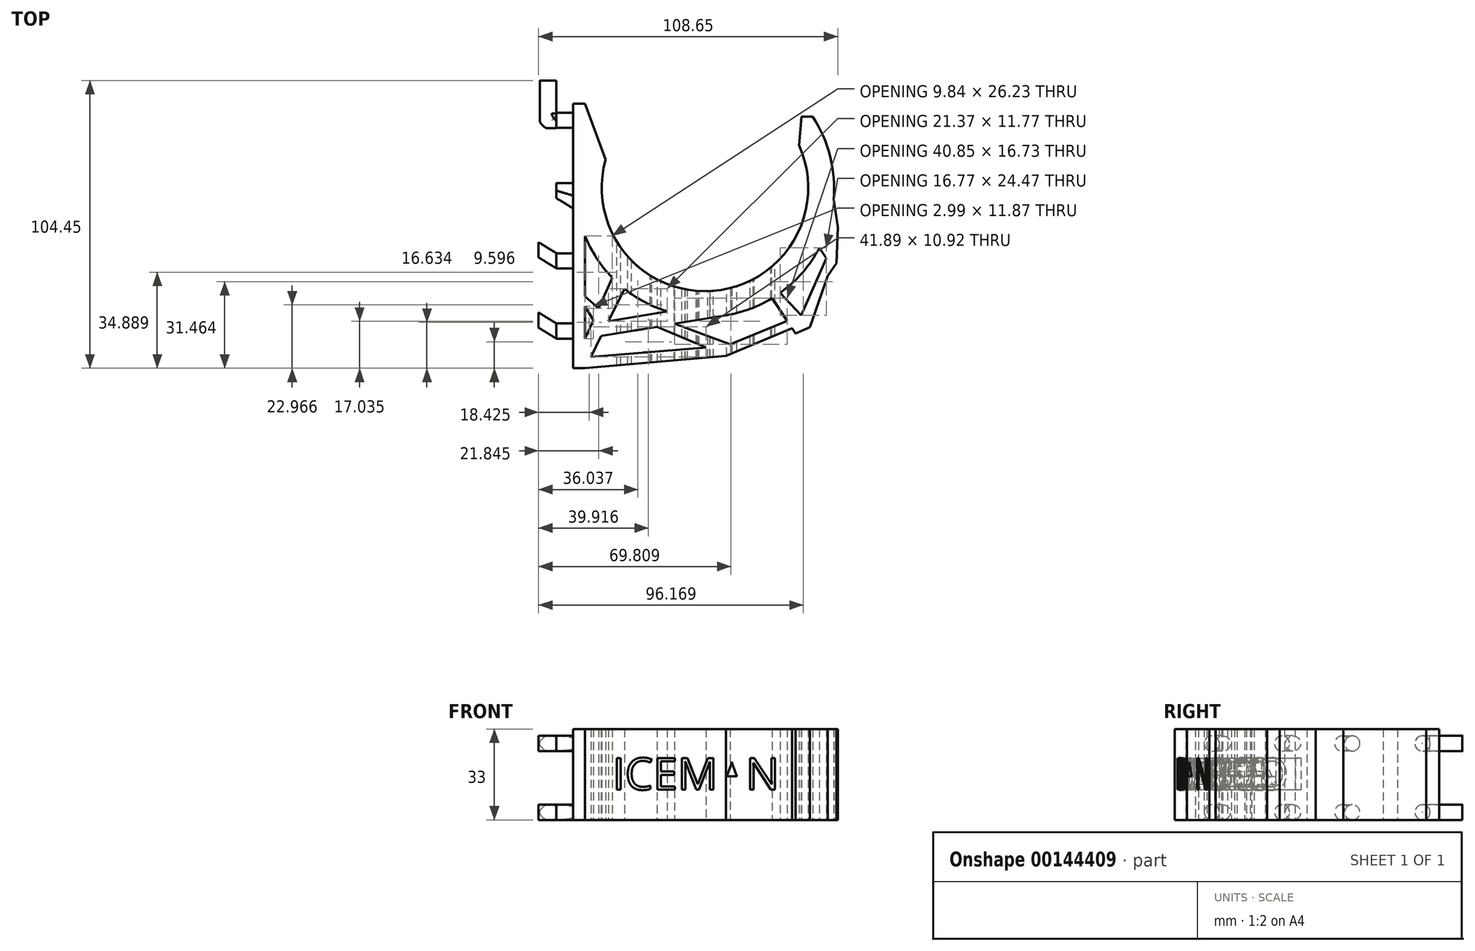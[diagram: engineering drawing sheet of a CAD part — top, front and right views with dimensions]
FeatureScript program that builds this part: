
annotation { "Feature Type Name" : "Feature", "Feature Type Description" : "" }
export const myFeature = defineFeature(function(context is Context, id is Id, definition is map)
    precondition{}
    {
        {
            var Q0;
            Q0=qCreatedBy(makeId("Top.planeOp"),FACE);
            var sketch = newSketch(context, id + "F0", { "sketchPlane" : qUnion([Q0])});
            skLineSegment(sketch, "E0.top", {"start": v(0, 33.67) * mm, "end": v(4.44, 33.67) * mm});
            skLineSegment(sketch, "E0.left", {"start": v(0, 0) * mm, "end": v(0, 33.67) * mm});
            skLineSegment(sketch, "E0.right", {"start": v(4.44, -16.05) * mm, "end": v(4.44, -14.33) * mm});
            skArc(sketch, "E1", {"start": v(11.88, 13.42) * mm, "mid": v(50.67, -34.27) * mm, "end": v(82.12, 18.55) * mm});
            skArc(sketch, "E2", {"start": v(4.44, -14.33) * mm, "mid": v(16.23, -31.39) * mm, "end": v(34.23, -41.69) * mm});
            skLineSegment(sketch, "E3", {"start": v(4.44, 33.67) * mm, "end": v(11.88, 13.42) * mm});
            skLineSegment(sketch, "E4", {"start": v(83.02, 29.02) * mm, "end": v(87.01, 29.02) * mm});
            skLineSegment(sketch, "E5.top", {"start": v(0, -62.33) * mm, "end": v(4.44, -62.33) * mm});
            skLineSegment(sketch, "E5.left", {"start": v(0, 33.67) * mm, "end": v(0, -62.33) * mm});
            skLineSegment(sketch, "E5.right", {"start": v(4.44, -14.33) * mm, "end": v(4.44, -36.24) * mm});
            skLineSegment(sketch, "E6", {"start": v(14.27, -29.48) * mm, "end": v(9.36, -40.56) * mm});
            skLineSegment(sketch, "E7", {"start": v(10.19, -50.67) * mm, "end": v(30.6, -47.27) * mm});
            skLineSegment(sketch, "E8", {"start": v(55.64, -43.1) * mm, "end": v(76.36, -43.1) * mm});
            skLineSegment(sketch, "E9", {"start": v(83.02, 29.02) * mm, "end": v(82.12, 18.55) * mm});
            skLineSegment(sketch, "E10", {"start": v(18.67, -33.48) * mm, "end": v(12.86, -45.25) * mm});
            skLineSegment(sketch, "E11", {"start": v(12.86, -45.25) * mm, "end": v(34.23, -41.69) * mm});
            skLineSegment(sketch, "E12", {"start": v(36.9, -46.22) * mm, "end": v(57.12, -53.66) * mm});
            skLineSegment(sketch, "E13", {"start": v(48.37, -54.8) * mm, "end": v(30.6, -47.27) * mm});
            skLineSegment(sketch, "E14", {"start": v(30.6, -47.27) * mm, "end": v(48.37, -54.8) * mm});
            skLineSegment(sketch, "E15", {"start": v(57.12, -53.66) * mm, "end": v(77.74, -45.18) * mm});
            skLineSegment(sketch, "E16.trimOffspring", {"start": v(36.9, -46.22) * mm, "end": v(55.64, -43.1) * mm});
            skArc(sketch, "E17.trimOffspring", {"start": v(55.64, -43.1) * mm, "mid": v(64.25, -40.8) * mm, "end": v(72.27, -36.93) * mm});
            skLineSegment(sketch, "E18", {"start": v(82.8, -43.1) * mm, "end": v(75.3, -34.93) * mm});
            skLineSegment(sketch, "E19", {"start": v(72.27, -36.93) * mm, "end": v(77.74, -45.18) * mm});
            skLineSegment(sketch, "E20", {"start": v(86.04, -47.4) * mm, "end": v(92.47, -28.8) * mm});
            skLineSegment(sketch, "E21", {"start": v(97.82, -6.72) * mm, "end": v(94.7, 0) * mm});
            skLineSegment(sketch, "E22", {"start": v(89.45, -18.63) * mm, "end": v(92.06, -22.39) * mm});
            skLineSegment(sketch, "E23.trimOffspring", {"start": v(79.52, -47.86) * mm, "end": v(80.77, -49.75) * mm});
            skLineSegment(sketch, "E24", {"start": v(97.82, -6.72) * mm, "end": v(93.84, -6.35) * mm});
            skLineSegment(sketch, "E25", {"start": v(7.43, -44.89) * mm, "end": v(4.44, -39.76) * mm});
            skLineSegment(sketch, "E26", {"start": v(4.44, -36.24) * mm, "end": v(9.36, -40.56) * mm});
            skLineSegment(sketch, "E27", {"start": v(94.62, -1.13) * mm, "end": v(96.16, -11.08) * mm});
            skLineSegment(sketch, "E28", {"start": v(95.7, -24.2) * mm, "end": v(94.3, -26.43) * mm});
            skLineSegment(sketch, "E29", {"start": v(96.16, -11.08) * mm, "end": v(95.7, -24.2) * mm});
            skPoint(sketch, "E30.orphan", {"position": v(97.7, -21.03) * mm});
            skArc(sketch, "E31.trimOffspring", {"start": v(94.62, -1.13) * mm, "mid": v(93.39, 14.6) * mm, "end": v(87.01, 29.02) * mm});
            skArc(sketch, "E32.trimOffspring", {"start": v(94.7, 0) * mm, "mid": v(1.5, 9.46) * mm, "end": v(93.84, -6.35) * mm});
            skLineSegment(sketch, "E33", {"start": v(82.8, -43.1) * mm, "end": v(92.06, -22.39) * mm});
            skLineSegment(sketch, "E34", {"start": v(92.47, -28.8) * mm, "end": v(95.7, -24.2) * mm});
            skLineSegment(sketch, "E35.trimOffspring", {"start": v(79.52, -47.86) * mm, "end": v(55.58, -57.85) * mm});
            skLineSegment(sketch, "E36", {"start": v(80.77, -49.75) * mm, "end": v(86.04, -47.4) * mm});
            skArc(sketch, "E37.trimOffspring", {"start": v(75.3, -34.93) * mm, "mid": v(83.32, -27.6) * mm, "end": v(89.45, -18.63) * mm});
            skLineSegment(sketch, "E38.trimOffspring", {"start": v(7.43, -44.89) * mm, "end": v(4.44, -51.63) * mm});
            skLineSegment(sketch, "E39.trimOffspring", {"start": v(10.19, -50.67) * mm, "end": v(6.48, -58.2) * mm});
            skLineSegment(sketch, "E40.trimOffspring", {"start": v(4.44, -39.76) * mm, "end": v(4.44, -51.63) * mm});
            skLineSegment(sketch, "E41", {"start": v(4.44, -62.33) * mm, "end": v(55.58, -57.85) * mm});
            skLineSegment(sketch, "E42", {"start": v(6.48, -58.2) * mm, "end": v(48.37, -54.8) * mm});
            skSolve(sketch);
        }
        {
            var Q0;
            {var subQ9=sQuery(id+"F0.wireOp",EDGE,"E1");Q0=makeQuery(id+"F0.imprint","IMPRINT",FACE,{"disambiguationData":[TD([[makeQuery(id+"F0.imprint","IMPRINT",EDGE,{"derivedFrom":subQ9}),-1.0]])]});}
            var Q1;
            {var subQ14=sQuery(id+"F0.wireOp",EDGE,"E0.top");Q1=makeQuery(id+"F0.imprint","IMPRINT",FACE,{"disambiguationData":[TD([[makeQuery(id+"F0.imprint","IMPRINT",EDGE,{"derivedFrom":subQ14}),-1.0]])]});}
            extrude(context, id + "F1", {"entities" : qUnion([Q0, Q1]), "depth" : 33 * mm});
        }
        {
            var Q0;
            Q0=makeQuery(id+"F1.opExtrude","SWEPT_FACE",FACE,{"disambiguationData":[OSD([sQuery(id+"F0.wireOp",EDGE,"E5.left")])]});
            var sketch = newSketch(context, id + "F2", { "sketchPlane" : qUnion([Q0])});
            skLineSegment(sketch, "E43.bottom", {"start": v(-27.67, 27.75) * mm, "end": v(23.33, 27.75) * mm, "construction": true});
            skLineSegment(sketch, "E43.top", {"start": v(-27.67, 2.75) * mm, "end": v(23.33, 2.75) * mm, "construction": true});
            skLineSegment(sketch, "E43.left", {"start": v(-27.67, 27.75) * mm, "end": v(-27.67, 2.75) * mm, "construction": true});
            skLineSegment(sketch, "E43.right", {"start": v(23.33, 27.75) * mm, "end": v(23.33, 2.75) * mm, "construction": true});
            skCircle(sketch, "E44", {"center": v(-27.67, 2.75) * mm, "radius": 2.75 * mm});
            skCircle(sketch, "E45", {"center": v(-27.67, 27.75) * mm, "radius": 2.75 * mm});
            skCircle(sketch, "E46", {"center": v(23.33, 27.75) * mm, "radius": 2.75 * mm});
            skCircle(sketch, "E47", {"center": v(23.33, 2.75) * mm, "radius": 2.75 * mm});
            skCircle(sketch, "E48", {"center": v(-2.17, 2.75) * mm, "radius": 2.75 * mm});
            skCircle(sketch, "E49", {"center": v(-2.17, 27.75) * mm, "radius": 2.75 * mm});
            skLineSegment(sketch, "E50", {"start": v(-27.67, 2.75) * mm, "end": v(69.72, 2.75) * mm, "construction": true});
            skLineSegment(sketch, "E51", {"start": v(69.72, 2.75) * mm, "end": v(69.72, 27.75) * mm, "construction": true});
            skLineSegment(sketch, "E52", {"start": v(69.72, 27.75) * mm, "end": v(-42.83, 27.75) * mm, "construction": true});
            skCircle(sketch, "E53", {"center": v(48.83, 2.75) * mm, "radius": 2.75 * mm});
            skCircle(sketch, "E54", {"center": v(48.83, 27.75) * mm, "radius": 2.75 * mm});
            skSolve(sketch);
        }
        {
            var Q0;
            Q0 = qSketchRegion(id + "F2", true);
            extrude(context, id + "F3", {"entities" : qUnion([Q0]), "operationType" : NewBodyOperationType.ADD, "depth" : 6 * mm});
        }
        {
            var Q0;
            Q0=makeQuery(id+"F3.opExtrude","CAP_FACE",FACE,{"disambiguationData":[OSD([sQuery(id+"F2.wireOp",EDGE,"E44")])],"isStart":false});
            var sketch = newSketch(context, id + "F4", { "sketchPlane" : qUnion([Q0])});
            skLineSegment(sketch, "E55", {"start": v(-27.67, 2.75) * mm, "end": v(-27.67, 27.75) * mm});
            skArc(sketch, "E56", {"start": v(-24.92, 2.75) * mm, "mid": v(-27.67, 5.5) * mm, "end": v(-30.42, 2.75) * mm});
            skCircle(sketch, "E57", {"center": v(-27.67, 27.75) * mm, "radius": 2.82 * mm});
            skLineSegment(sketch, "E58.bottom", {"start": v(-27.67, 2.75) * mm, "end": v(-30.42, 2.75) * mm});
            skLineSegment(sketch, "E58.top", {"start": v(-24.92, 0) * mm, "end": v(-42.12, 0) * mm});
            skLineSegment(sketch, "E58.right", {"start": v(-42.12, 2.75) * mm, "end": v(-42.12, 0) * mm});
            skLineSegment(sketch, "E59.top", {"start": v(-42.12, 5.5) * mm, "end": v(-27.67, 5.5) * mm});
            skLineSegment(sketch, "E59.left", {"start": v(-42.12, 0) * mm, "end": v(-42.12, 5.5) * mm});
            skLineSegment(sketch, "E60.bottom", {"start": v(-27.67, 27.75) * mm, "end": v(-30.48, 27.75) * mm});
            skLineSegment(sketch, "E60.top", {"start": v(-27.67, 24.93) * mm, "end": v(-42.12, 24.93) * mm});
            skLineSegment(sketch, "E60.left", {"start": v(-27.67, 27.75) * mm, "end": v(-27.67, 24.93) * mm});
            skLineSegment(sketch, "E60.right", {"start": v(-42.12, 27.75) * mm, "end": v(-42.12, 24.93) * mm});
            skLineSegment(sketch, "E61.bottom", {"start": v(-42.12, 24.93) * mm, "end": v(-27.67, 24.93) * mm});
            skLineSegment(sketch, "E61.top", {"start": v(-42.12, 30.57) * mm, "end": v(-27.67, 30.57) * mm});
            skLineSegment(sketch, "E61.left", {"start": v(-42.12, 24.93) * mm, "end": v(-42.12, 30.57) * mm});
            skPoint(sketch, "E62.orphan", {"position": v(-24.92, 5.5) * mm});
            skSolve(sketch);
        }
        {
            var Q0;
            Q0 = qSketchRegion(id + "F4", true);
            var Q1;
            {var subQ6=sQuery(id+"F4.wireOp",EDGE,"E59.top");Q1=makeQuery(id+"F4.imprint","IMPRINT",FACE,{"disambiguationData":[TD([[makeQuery(id+"F4.imprint","IMPRINT",EDGE,{"derivedFrom":subQ6}),-1.0]])]});}
            var Q2;
            {var subQ6=sQuery(id+"F4.wireOp",EDGE,"E58.bottom");Q2=makeQuery(id+"F4.imprint","IMPRINT",FACE,{"disambiguationData":[TD([[makeQuery(id+"F4.imprint","IMPRINT",EDGE,{"derivedFrom":subQ6}),1.0]])]});}
            extrude(context, id + "F5", {"entities" : qUnion([Q0, Q1, Q2]), "operationType" : NewBodyOperationType.ADD, "depth" : 6 * mm});
        }
        {
            var Q0;
            Q0=makeQuery(id+"F5.opExtrude","CAP_EDGE",EDGE,{"disambiguationData":[OSD([sQuery(id+"F2.wireOp",EDGE,"E44"),sQuery(id+"F4.wireOp",EDGE,"E56")])],"isStart":false});
            var Q1;
            Q1=makeQuery(id+"F5.opExtrude","CAP_EDGE",EDGE,{"disambiguationData":[OSD([sQuery(id+"F4.wireOp",EDGE,"E57")])],"isStart":false});
            chamfer(context, id + "F6", {"entities" : qUnion([Q0, Q1]), "chamferType" : ChamferType.OFFSET_ANGLE, "width" : 2 * mm, "oppositeDirection" : false, "angle" : 45 * degree, "tangentPropagation" : true});
        }
        {
            var Q0;
            Q0=makeQuery(id+"F5.opExtrude","CAP_EDGE",EDGE,{"disambiguationData":[OSD([sQuery(id+"F4.wireOp",EDGE,"E58.top")])],"isStart":true});
            var Q1;
            Q1=makeQuery(id+"F5.opExtrude","CAP_EDGE",EDGE,{"disambiguationData":[OSD([sQuery(id+"F4.wireOp",EDGE,"E61.bottom")])],"isStart":true});
            var Q2;
            {var subQ0=sQuery(id+"F4.wireOp",EDGE,"E61.bottom");Q2=makeQuery(id+"F6.opChamfer","BLEND_EDGE",EDGE,{"blendedFrom":[makeQuery(id+"F5.opExtrude","CAP_EDGE",EDGE,{"disambiguationData":[OSD([subQ0])],"isStart":false}),makeQuery(id+"F5.opExtrude","SWEPT_FACE",FACE,{"disambiguationData":[OSD([subQ0])]})],"blendedInto":[makeQuery(id+"F5.opExtrude","SWEPT_FACE",FACE,{"disambiguationData":[OSD([subQ0])]})]});}
            var Q3;
            {var subQ0=sQuery(id+"F4.wireOp",EDGE,"E61.bottom");Q3=makeQuery(id+"F6.opChamfer","BLEND_EDGE",EDGE,{"blendedFrom":[makeQuery(id+"F5.opExtrude","CAP_EDGE",EDGE,{"disambiguationData":[OSD([subQ0])],"isStart":false}),makeQuery(id+"F5.opExtrude","CAP_FACE",FACE,{"disambiguationData":[OSD([sQuery(id+"F4.wireOp",EDGE,"E57"),subQ0,sQuery(id+"F4.wireOp",EDGE,"E61.top"),sQuery(id+"F4.wireOp",EDGE,"E61.left")])],"isStart":false})],"blendedInto":[makeQuery(id+"F5.opExtrude","CAP_FACE",FACE,{"disambiguationData":[OSD([sQuery(id+"F4.wireOp",EDGE,"E57"),subQ0,sQuery(id+"F4.wireOp",EDGE,"E61.top"),sQuery(id+"F4.wireOp",EDGE,"E61.left")])],"isStart":false})]});}
            var Q4;
            {var subQ0=sQuery(id+"F4.wireOp",EDGE,"E58.top");Q4=makeQuery(id+"F6.opChamfer","BLEND_EDGE",EDGE,{"blendedFrom":[makeQuery(id+"F5.opExtrude","CAP_EDGE",EDGE,{"disambiguationData":[OSD([subQ0])],"isStart":false}),makeQuery(id+"F5.opExtrude","SWEPT_FACE",FACE,{"disambiguationData":[OSD([subQ0])]})],"blendedInto":[makeQuery(id+"F5.opExtrude","SWEPT_FACE",FACE,{"disambiguationData":[OSD([subQ0])]})]});}
            var Q5;
            {var subQ0=sQuery(id+"F4.wireOp",EDGE,"E58.top");Q5=makeQuery(id+"F6.opChamfer","BLEND_EDGE",EDGE,{"blendedFrom":[makeQuery(id+"F5.opExtrude","CAP_EDGE",EDGE,{"disambiguationData":[OSD([subQ0])],"isStart":false}),makeQuery(id+"F5.opExtrude","CAP_FACE",FACE,{"disambiguationData":[OSD([sQuery(id+"F2.wireOp",EDGE,"E44"),sQuery(id+"F4.wireOp",EDGE,"E56"),subQ0,sQuery(id+"F4.wireOp",EDGE,"E59.top"),sQuery(id+"F4.wireOp",EDGE,"E59.left")])],"isStart":false})],"blendedInto":[makeQuery(id+"F5.opExtrude","CAP_FACE",FACE,{"disambiguationData":[OSD([sQuery(id+"F2.wireOp",EDGE,"E44"),sQuery(id+"F4.wireOp",EDGE,"E56"),subQ0,sQuery(id+"F4.wireOp",EDGE,"E59.top"),sQuery(id+"F4.wireOp",EDGE,"E59.left")])],"isStart":false})]});}
            var Q6;
            Q6=makeQuery(id+"F5.opExtrude","CAP_EDGE",EDGE,{"disambiguationData":[OSD([sQuery(id+"F4.wireOp",EDGE,"E59.top")])],"isStart":true});
            var Q7;
            {var subQ0=sQuery(id+"F4.wireOp",EDGE,"E61.top");Q7=makeQuery(id+"F6.opChamfer","BLEND_EDGE",EDGE,{"blendedFrom":[makeQuery(id+"F5.opExtrude","CAP_EDGE",EDGE,{"disambiguationData":[OSD([subQ0])],"isStart":false}),makeQuery(id+"F5.opExtrude","SWEPT_FACE",FACE,{"disambiguationData":[OSD([subQ0])]})],"blendedInto":[makeQuery(id+"F5.opExtrude","SWEPT_FACE",FACE,{"disambiguationData":[OSD([subQ0])]})]});}
            var Q8;
            {var subQ0=sQuery(id+"F4.wireOp",EDGE,"E61.top");Q8=makeQuery(id+"F6.opChamfer","BLEND_EDGE",EDGE,{"blendedFrom":[makeQuery(id+"F5.opExtrude","CAP_EDGE",EDGE,{"disambiguationData":[OSD([subQ0])],"isStart":false}),makeQuery(id+"F5.opExtrude","CAP_FACE",FACE,{"disambiguationData":[OSD([sQuery(id+"F4.wireOp",EDGE,"E57"),sQuery(id+"F4.wireOp",EDGE,"E61.bottom"),subQ0,sQuery(id+"F4.wireOp",EDGE,"E61.left")])],"isStart":false})],"blendedInto":[makeQuery(id+"F5.opExtrude","CAP_FACE",FACE,{"disambiguationData":[OSD([sQuery(id+"F4.wireOp",EDGE,"E57"),sQuery(id+"F4.wireOp",EDGE,"E61.bottom"),subQ0,sQuery(id+"F4.wireOp",EDGE,"E61.left")])],"isStart":false})]});}
            var Q9;
            {var subQ0=sQuery(id+"F4.wireOp",EDGE,"E59.top");Q9=makeQuery(id+"F6.opChamfer","BLEND_EDGE",EDGE,{"blendedFrom":[makeQuery(id+"F5.opExtrude","CAP_EDGE",EDGE,{"disambiguationData":[OSD([subQ0])],"isStart":false}),makeQuery(id+"F5.opExtrude","SWEPT_FACE",FACE,{"disambiguationData":[OSD([subQ0])]})],"blendedInto":[makeQuery(id+"F5.opExtrude","SWEPT_FACE",FACE,{"disambiguationData":[OSD([subQ0])]})]});}
            var Q10;
            Q10=makeQuery(id+"F5.opExtrude","CAP_EDGE",EDGE,{"disambiguationData":[OSD([sQuery(id+"F4.wireOp",EDGE,"E61.top")])],"isStart":true});
            fillet(context, id + "F7", {"entities" : qUnion([Q0, Q1, Q2, Q3, Q4, Q5, Q6, Q7, Q8, Q9, Q10]), "radius" : 1.66 * mm, "tangentPropagation" : true, "rho" : 0.5, "crossSection" : FilletCrossSection.CONIC, "allowEdgeOverflow" : false});
        }
        {
            var Q0;
            Q0=qCreatedBy(makeId("Front.planeOp"),FACE);
            var sketch = newSketch(context, id + "F8", { "sketchPlane" : qUnion([Q0])});
            skText(sketch, "E63", { "text": "ICEMAN\n", "fontName": "OpenSans-Regular.ttf"});
            const initialGuessF8  = {"E63": [0.01442, 0.01096, 1, 0, 0.0116]};
            skSetInitialGuess(sketch, initialGuessF8);
            skSolve(sketch);
        }
        {
            var Q0;
            Q0=makeQuery(id+"F8.imprint","IMPRINT",FACE,{"disambiguationData":[TD([[makeQuery(id+"F8.imprint","IMPRINT",EDGE,{"derivedFrom":sQuery(id+"F8.wireOp",EDGE,"E63.sketch_text.stroke-57")}),1.0]])]});
            var Q1;
            Q1=makeQuery(id+"F8.imprint","IMPRINT",FACE,{"disambiguationData":[TD([[makeQuery(id+"F8.imprint","IMPRINT",EDGE,{"derivedFrom":sQuery(id+"F8.wireOp",EDGE,"E63.sketch_text.stroke-62")}),-1.0]])]});
            var Q2;
            Q2=makeQuery(id+"F8.imprint","IMPRINT",FACE,{"disambiguationData":[TD([[makeQuery(id+"F8.imprint","IMPRINT",EDGE,{"derivedFrom":sQuery(id+"F8.wireOp",EDGE,"E63.sketch_text.stroke-31")}),-1.0]])]});
            var Q3;
            Q3=makeQuery(id+"F8.imprint","IMPRINT",FACE,{"disambiguationData":[TD([[makeQuery(id+"F8.imprint","IMPRINT",EDGE,{"derivedFrom":sQuery(id+"F8.wireOp",EDGE,"E63.sketch_text.stroke-19")}),-1.0]])]});
            var Q4;
            Q4=makeQuery(id+"F8.imprint","IMPRINT",FACE,{"disambiguationData":[TD([[makeQuery(id+"F8.imprint","IMPRINT",EDGE,{"derivedFrom":sQuery(id+"F8.wireOp",EDGE,"E63.sketch_text.stroke-4")}),-1.0]])]});
            var Q5;
            Q5=makeQuery(id+"F8.imprint","IMPRINT",FACE,{"disambiguationData":[TD([[makeQuery(id+"F8.imprint","IMPRINT",EDGE,{"derivedFrom":sQuery(id+"F8.wireOp",EDGE,"E63.sketch_text.stroke-0")}),-1.0]])]});
            extrude(context, id + "F9", {"entities" : qUnion([Q0, Q1, Q2, Q3, Q4, Q5]), "operationType" : NewBodyOperationType.REMOVE, "endBound" : BoundingType.THROUGH_ALL, "depth" : 25 * mm});
        }
        {
            var Q0;
            Q0=qCreatedBy(makeId("Top.planeOp"),FACE);
            var sketch = newSketch(context, id + "F10", { "sketchPlane" : qUnion([Q0])});
            skLineSegment(sketch, "E64", {"start": v(-6.13, 2.02) * mm, "end": v(-11.87, 7.9) * mm});
            skLineSegment(sketch, "E65", {"start": v(-6.28, -23.5) * mm, "end": v(-12.77, -19.53) * mm});
            skLineSegment(sketch, "E66", {"start": v(-6.4, -49.11) * mm, "end": v(-13.68, -47.32) * mm});
            skPoint(sketch, "E67.orphan", {"position": v(-13.68, -18.97) * mm});
            skSolve(sketch);
        }
        {
            var Q0;
            Q0=makeQuery(id+"F3.opExtrude","CAP_FACE",FACE,{"disambiguationData":[OSD([sQuery(id+"F2.wireOp",EDGE,"E46")])],"isStart":false});
            var Q1;
            Q1=makeQuery(id+"F3.opExtrude","CAP_FACE",FACE,{"disambiguationData":[OSD([sQuery(id+"F2.wireOp",EDGE,"E54")])],"isStart":false});
            var Q2;
            Q2=makeQuery(id+"F3.opExtrude","CAP_FACE",FACE,{"disambiguationData":[OSD([sQuery(id+"F2.wireOp",EDGE,"E47")])],"isStart":false});
            var Q3;
            Q3=makeQuery(id+"F3.opExtrude","CAP_FACE",FACE,{"disambiguationData":[OSD([sQuery(id+"F2.wireOp",EDGE,"E49")])],"isStart":false});
            var Q4;
            Q4=makeQuery(id+"F3.opExtrude","CAP_FACE",FACE,{"disambiguationData":[OSD([sQuery(id+"F2.wireOp",EDGE,"E48")])],"isStart":false});
            var Q5;
            Q5=makeQuery(id+"F3.opExtrude","CAP_FACE",FACE,{"disambiguationData":[OSD([sQuery(id+"F2.wireOp",EDGE,"E53")])],"isStart":false});
            var Q6;
            Q6=sQuery(id+"F10.wireOp",EDGE,"E65");
            sweep(context, id + "F11", {"operationType" : NewBodyOperationType.ADD, "profiles" : qUnion([Q0, Q1, Q2, Q3, Q4, Q5]), "path" : qUnion([Q6])});
        }
    });
